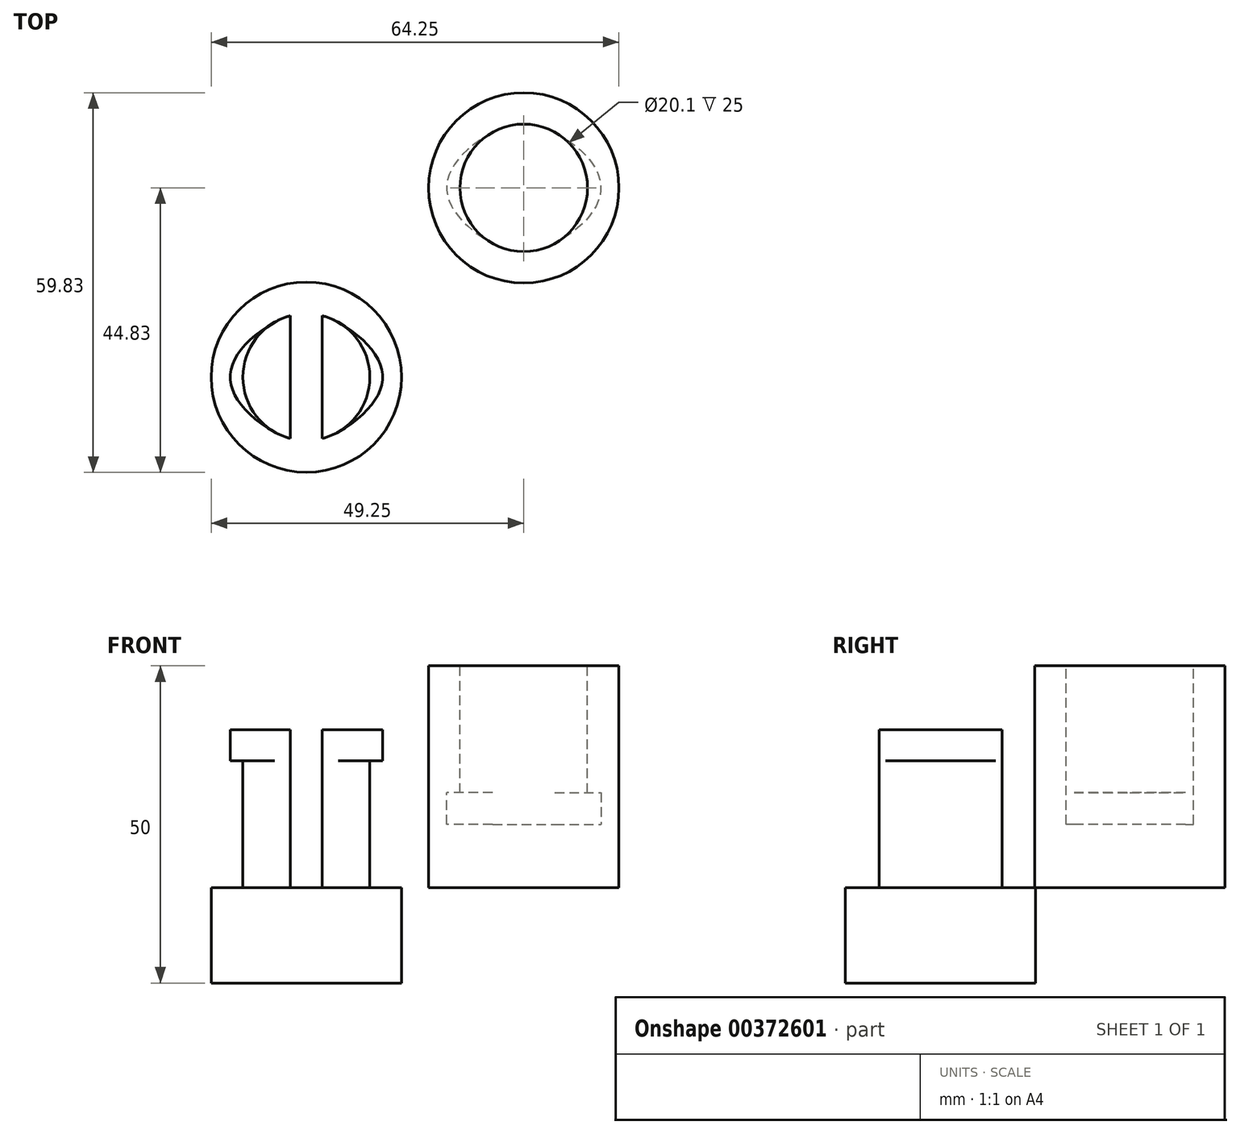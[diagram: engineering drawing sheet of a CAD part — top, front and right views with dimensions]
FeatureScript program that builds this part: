
annotation { "Feature Type Name" : "Feature", "Feature Type Description" : "" }
export const myFeature = defineFeature(function(context is Context, id is Id, definition is map)
    precondition{}
    {
        {
            var Q0;
            Q0=qCreatedBy(makeId("Top.planeOp"),FACE);
            var sketch = newSketch(context, id + "F0", { "sketchPlane" : qUnion([Q0])});
            skCircle(sketch, "E0", {"center": v(0, 0) * mm, "radius": 15 * mm});
            skSolve(sketch);
        }
        {
            var Q0;
            Q0=makeQuery(id+"F0.imprint","IMPRINT",FACE,{"disambiguationData":[TD([[makeQuery(id+"F0.imprint","IMPRINT",EDGE,{"derivedFrom":sQuery(id+"F0.wireOp",EDGE,"E0")}),1.0]])]});
            extrude(context, id + "F1", {"entities" : qUnion([Q0]), "depth" : 35 * mm});
        }
        {
            var Q0;
            Q0=makeQuery(id+"F1.opExtrude","CAP_FACE",FACE,{"disambiguationData":[OSD([sQuery(id+"F0.wireOp",EDGE,"E0")])],"isStart":false});
            var sketch = newSketch(context, id + "F2", { "sketchPlane" : qUnion([Q0])});
            skCircle(sketch, "E1", {"center": v(0, 0) * mm, "radius": 10.05 * mm});
            skSolve(sketch);
        }
        {
            var Q0;
            Q0=makeQuery(id+"F2.imprint","IMPRINT",FACE,{"disambiguationData":[TD([[makeQuery(id+"F2.imprint","IMPRINT",EDGE,{"derivedFrom":sQuery(id+"F2.wireOp",EDGE,"E1")}),1.0]])]});
            extrude(context, id + "F3", {"entities" : qUnion([Q0]), "operationType" : NewBodyOperationType.REMOVE, "oppositeDirection" : true, "depth" : 25 * mm});
        }
        {
            var Q0;
            Q0=qCreatedBy(makeId("Top.planeOp"),FACE);
            var sketch = newSketch(context, id + "F4", { "sketchPlane" : qUnion([Q0])});
            skArc(sketch, "E2", {"start": v(-31.75, -39.52) * mm, "mid": v(-24.25, -29.83) * mm, "end": v(-31.75, -20.15) * mm});
            skLineSegment(sketch, "E3", {"start": v(-36.75, -20.15) * mm, "end": v(-36.75, -39.52) * mm});
            skLineSegment(sketch, "E4", {"start": v(-31.75, -20.15) * mm, "end": v(-31.75, -39.52) * mm});
            skArc(sketch, "E5.trimOffspring", {"start": v(-36.75, -20.15) * mm, "mid": v(-44.25, -29.83) * mm, "end": v(-36.75, -39.52) * mm});
            skSolve(sketch);
        }
        {
            var Q0;
            Q0 = qSketchRegion(id + "F4", true);
            extrude(context, id + "F5", {"entities" : qUnion([Q0]), "depth" : 24.9 * mm});
        }
        {
            var Q0;
            Q0=qCreatedBy(makeId("Top.planeOp"),FACE);
            var sketch = newSketch(context, id + "F6", { "sketchPlane" : qUnion([Q0])});
            skCircle(sketch, "E6", {"center": v(-34.25, -29.83) * mm, "radius": 15 * mm});
            skSolve(sketch);
        }
        {
            var Q0;
            Q0 = qSketchRegion(id + "F6", true);
            extrude(context, id + "F7", {"entities" : qUnion([Q0]), "operationType" : NewBodyOperationType.ADD, "oppositeDirection" : true, "depth" : 15 * mm});
        }
        {
            var Q0;
            Q0=makeQuery(id+"F5.opExtrude","CAP_FACE",FACE,{"disambiguationData":[OSD([sQuery(id+"F4.wireOp",EDGE,"E3"),sQuery(id+"F4.wireOp",EDGE,"E5.trimOffspring")])],"isStart":false});
            var sketch = newSketch(context, id + "F8", { "sketchPlane" : qUnion([Q0])});
            skFitSpline(sketch, "E7", {"points": [v(-39.25, -21.17) * mm, v(-46.25, -29.83) * mm, v(-39.25, -38.5) * mm], "startDerivative": vector(-25.98, -15) * mm, "endDerivative": vector(25.98, -15) * mm});
            skLineSegment(sketch, "E8", {"start": v(-44.25, -29.83) * mm, "end": v(-46.25, -29.83) * mm, "construction": true});
            skLineSegment(sketch, "E9", {"start": v(-34.25, -14.83) * mm, "end": v(-34.25, -44.83) * mm, "construction": true});
            skPoint(sketch, "E10", {"position": v(-34.25, -29.83) * mm});
            skLineSegment(sketch, "E11", {"start": v(-39.25, -21.17) * mm, "end": v(-43.58, -23.67) * mm, "construction": true});
            skLineSegment(sketch, "E12", {"start": v(-43.58, -36) * mm, "end": v(-39.25, -38.5) * mm, "construction": true});
            skLineSegment(sketch, "E13", {"start": v(-39.25, -38.5) * mm, "end": v(-39.25, -21.17) * mm, "construction": true});
            skArc(sketch, "E14.0", {"start": v(-39.25, -21.17) * mm, "mid": v(-44.25, -29.83) * mm, "end": v(-39.25, -38.5) * mm});
            skPoint(sketch, "E15.orphan", {"position": v(-36.75, -20.15) * mm});
            skPoint(sketch, "E16.orphan", {"position": v(-36.75, -39.52) * mm});
            skArc(sketch, "E17.MirrorCS", {"start": v(-29.25, -21.17) * mm, "mid": v(-24.25, -29.83) * mm, "end": v(-29.25, -38.5) * mm});
            skFitSpline(sketch, "E18.MirrorCS", {"points": [v(-29.25, -21.17) * mm, v(-22.25, -29.83) * mm, v(-29.25, -38.5) * mm], "startDerivative": vector(25.98, -15) * mm, "endDerivative": vector(-25.98, -15) * mm});
            skSolve(sketch);
        }
        {
            var Q0;
            Q0 = qSketchRegion(id + "F8", true);
            extrude(context, id + "F9", {"entities" : qUnion([Q0]), "operationType" : NewBodyOperationType.ADD, "oppositeDirection" : true, "depth" : 4.9 * mm});
        }
        {
            var Q0;
            Q0=makeQuery(id+"F3.boolean.opBoolean","COPY",FACE,{"derivedFrom":makeQuery(id+"F3.opExtrude","CAP_FACE",FACE,{"disambiguationData":[OSD([sQuery(id+"F2.wireOp",EDGE,"E1")])],"isStart":false})});
            var sketch = newSketch(context, id + "F10", { "sketchPlane" : qUnion([Q0])});
            skFitSpline(sketch, "E19", {"points": [v(-4.9, 8.77) * mm, v(-12.15, 0) * mm, v(-4.9, -8.77) * mm], "startDerivative": vector(-26.24, -14.54) * mm, "endDerivative": vector(26.24, -14.54) * mm});
            skLineSegment(sketch, "E20", {"start": v(0, 10.05) * mm, "end": v(0, -10.05) * mm, "construction": true});
            skLineSegment(sketch, "E21", {"start": v(-10.05, 0) * mm, "end": v(-12.15, 0) * mm, "construction": true});
            skLineSegment(sketch, "E22", {"start": v(-4.9, -8.77) * mm, "end": v(-4.9, 8.77) * mm, "construction": true});
            skLineSegment(sketch, "E23", {"start": v(-4.9, 8.77) * mm, "end": v(-9.27, 6.35) * mm, "construction": true});
            skLineSegment(sketch, "E24", {"start": v(-4.9, -8.77) * mm, "end": v(-9.27, -6.35) * mm, "construction": true});
            skArc(sketch, "E25.0", {"start": v(-4.9, 8.77) * mm, "mid": v(-10.05, 0) * mm, "end": v(-4.9, -8.77) * mm});
            skArc(sketch, "E26.MirrorCS", {"start": v(4.9, 8.77) * mm, "mid": v(10.05, 0) * mm, "end": v(4.9, -8.77) * mm});
            skFitSpline(sketch, "E27.MirrorCS", {"points": [v(4.9, 8.77) * mm, v(12.15, 0) * mm, v(4.9, -8.77) * mm], "startDerivative": vector(26.24, -14.54) * mm, "endDerivative": vector(-26.24, -14.54) * mm});
            skSolve(sketch);
        }
        {
            var Q0;
            Q0 = qSketchRegion(id + "F10", true);
            extrude(context, id + "F11", {"entities" : qUnion([Q0]), "operationType" : NewBodyOperationType.REMOVE, "depth" : 5 * mm});
        }
    });
